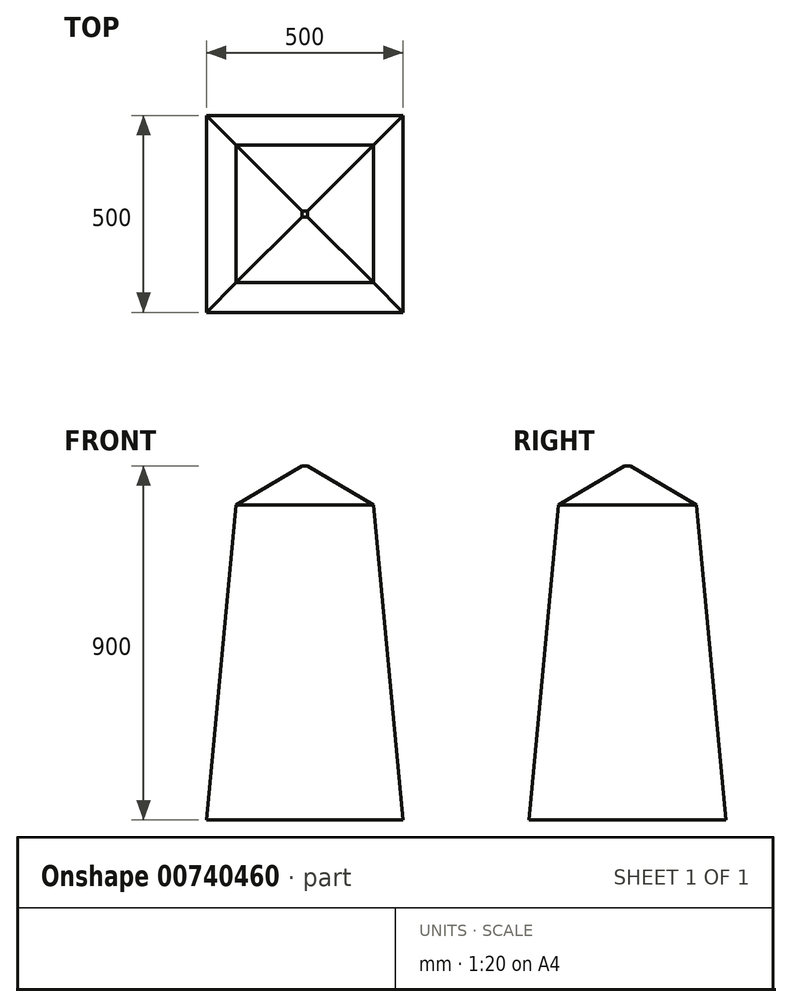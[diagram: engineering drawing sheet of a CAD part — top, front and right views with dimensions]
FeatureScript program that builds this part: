
annotation { "Feature Type Name" : "Feature", "Feature Type Description" : "" }
export const myFeature = defineFeature(function(context is Context, id is Id, definition is map)
    precondition{}
    {
        {
            var Q0;
            Q0=qCreatedBy(makeId("Top.planeOp"),FACE);
            var sketch = newSketch(context, id + "F0", { "sketchPlane" : qUnion([Q0])});
            skLineSegment(sketch, "E0.bottom", {"start": v(250, -250) * mm, "end": v(-250, -250) * mm});
            skLineSegment(sketch, "E0.top", {"start": v(250, 250) * mm, "end": v(-250, 250) * mm});
            skLineSegment(sketch, "E0.left", {"start": v(250, -250) * mm, "end": v(250, 250) * mm});
            skLineSegment(sketch, "E0.right", {"start": v(-250, -250) * mm, "end": v(-250, 250) * mm});
            skPoint(sketch, "E0.middle", {"position": v(0, 0) * mm});
            skSolve(sketch);
        }
        {
            var Q0;
            Q0=makeQuery(id+"F0.imprint","IMPRINT",FACE,{"disambiguationData":[TD([[makeQuery(id+"F0.imprint","IMPRINT",EDGE,{"derivedFrom":sQuery(id+"F0.wireOp",EDGE,"E0.bottom")}),-1.0]])]});
            cPlane(context, id + "F1", {"entities" : qUnion([Q0]), "cplaneType" : CPlaneType.OFFSET, "offset" : 800 * mm, "width" : 150 * mm, "height" : 150 * mm});
        }
        {
            var Q0;
            Q0=qCreatedBy(id+"F1.planeOp",FACE);
            var sketch = newSketch(context, id + "F2", { "sketchPlane" : qUnion([Q0])});
            skLineSegment(sketch, "E1.bottom", {"start": v(175, -175) * mm, "end": v(-175, -175) * mm});
            skLineSegment(sketch, "E1.top", {"start": v(175, 175) * mm, "end": v(-175, 175) * mm});
            skLineSegment(sketch, "E1.left", {"start": v(175, -175) * mm, "end": v(175, 175) * mm});
            skLineSegment(sketch, "E1.right", {"start": v(-175, -175) * mm, "end": v(-175, 175) * mm});
            skPoint(sketch, "E1.middle", {"position": v(0, 0) * mm});
            skSolve(sketch);
        }
        {
            var Q0;
            Q0=qCreatedBy(id+"F1.planeOp",FACE);
            cPlane(context, id + "F3", {"entities" : qUnion([Q0]), "cplaneType" : CPlaneType.OFFSET, "offset" : 100 * mm, "width" : 150 * mm, "height" : 150 * mm});
        }
        {
            var Q0;
            Q0=qCreatedBy(id+"F3.planeOp",FACE);
            var sketch = newSketch(context, id + "F4", { "sketchPlane" : qUnion([Q0])});
            skLineSegment(sketch, "E2.bottom", {"start": v(7.5, 7.5) * mm, "end": v(-7.5, 7.5) * mm});
            skLineSegment(sketch, "E2.top", {"start": v(7.5, -7.5) * mm, "end": v(-7.5, -7.5) * mm});
            skLineSegment(sketch, "E2.left", {"start": v(7.5, 7.5) * mm, "end": v(7.5, -7.5) * mm});
            skLineSegment(sketch, "E2.right", {"start": v(-7.5, 7.5) * mm, "end": v(-7.5, -7.5) * mm});
            skPoint(sketch, "E2.middle", {"position": v(0, 0) * mm});
            skSolve(sketch);
        }
        {
            var Q0;
            Q0=makeQuery(id+"F0.imprint","IMPRINT",FACE,{"disambiguationData":[TD([[makeQuery(id+"F0.imprint","IMPRINT",EDGE,{"derivedFrom":sQuery(id+"F0.wireOp",EDGE,"E0.bottom")}),-1.0]])]});
            var Q1;
            Q1=makeQuery(id+"F2.imprint","IMPRINT",FACE,{"disambiguationData":[TD([[makeQuery(id+"F2.imprint","IMPRINT",EDGE,{"derivedFrom":sQuery(id+"F2.wireOp",EDGE,"E1.bottom")}),-1.0]])]});
            loft(context, id + "F5", {"sheetProfilesArray" : [{ "sheetProfileEntities" : qUnion([Q0]) }, { "sheetProfileEntities" : qUnion([Q1]) }]});
        }
        {
            var Q1;
            Q1=makeQuery(id+"F5.opLoft","CAP_FACE",FACE,{"disambiguationData":[OSD([makeQuery(id+"F2.imprint","IMPRINT",FACE,{"disambiguationData":[TD([[makeQuery(id+"F2.imprint","IMPRINT",EDGE,{"derivedFrom":sQuery(id+"F2.wireOp",EDGE,"E1.bottom")}),-1.0]])]})])],"isStart":true});
            var Q2;
            Q2=makeQuery(id+"F4.imprint","IMPRINT",FACE,{"disambiguationData":[TD([[makeQuery(id+"F4.imprint","IMPRINT",EDGE,{"derivedFrom":sQuery(id+"F4.wireOp",EDGE,"E2.bottom")}),1.0]])]});
            loft(context, id + "F6", {"operationType" : NewBodyOperationType.ADD, "sheetProfilesArray" : [{ "sheetProfileEntities" : qUnion([Q1]) }, { "sheetProfileEntities" : qUnion([Q2]) }]});
        }
    });
